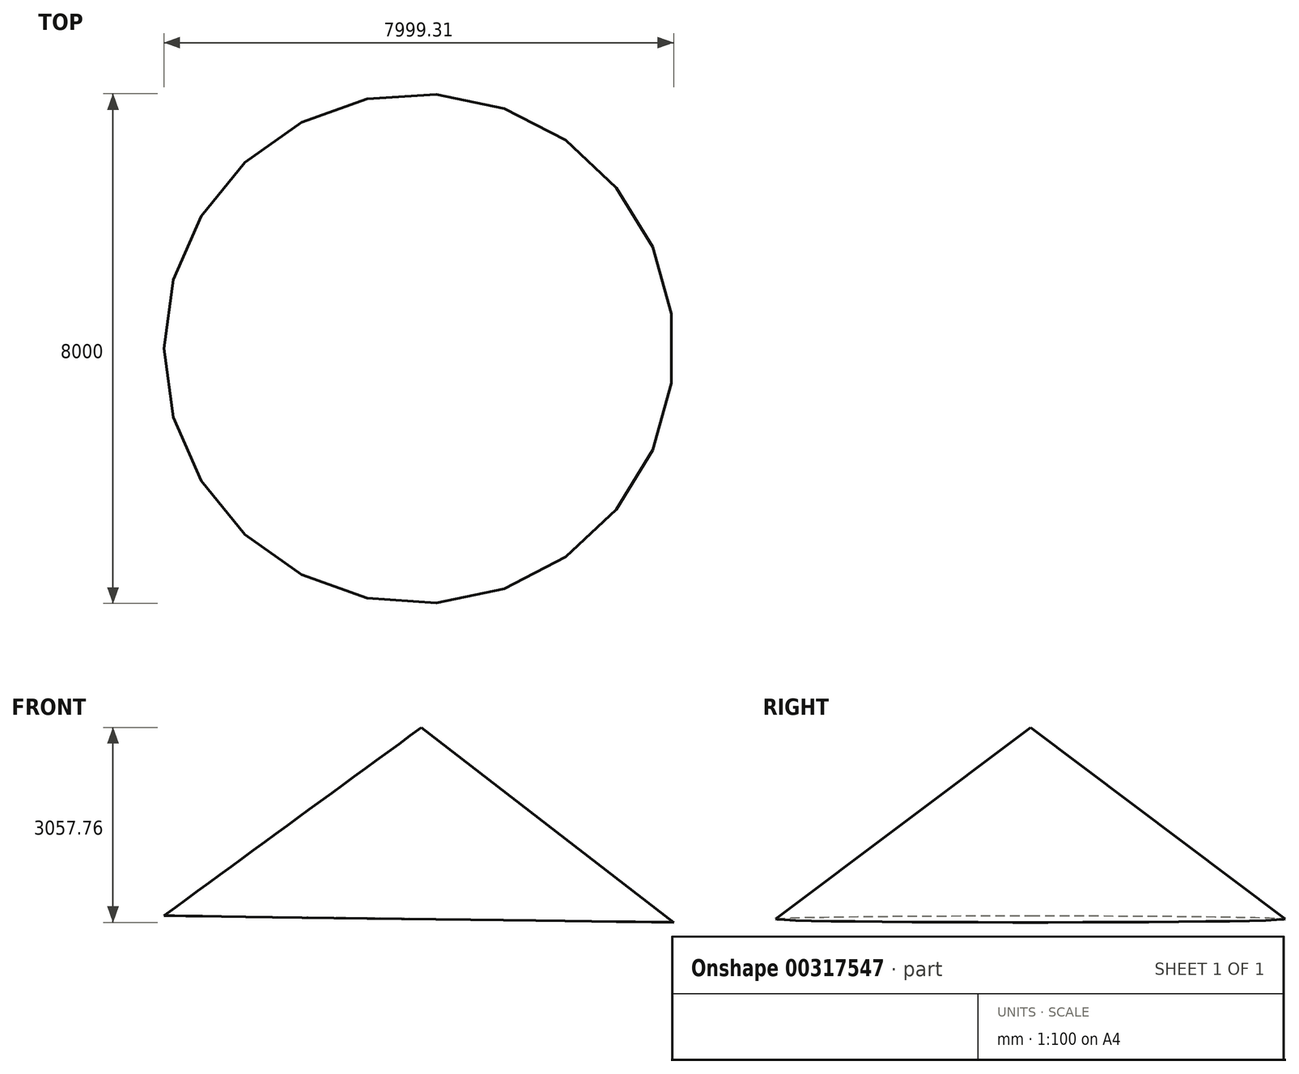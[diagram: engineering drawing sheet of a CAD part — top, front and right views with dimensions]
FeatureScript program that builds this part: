
annotation { "Feature Type Name" : "Feature", "Feature Type Description" : "" }
export const myFeature = defineFeature(function(context is Context, id is Id, definition is map)
    precondition{}
    {
        {
            var Q0;
            Q0=qCreatedBy(makeId("Front.planeOp"),FACE);
            var sketch = newSketch(context, id + "F0", { "sketchPlane" : qUnion([Q0])});
            skLineSegment(sketch, "E0", {"start": v(-48.48, -19.36) * mm, "end": v(-9.18, 2980.64) * mm});
            skLineSegment(sketch, "E1", {"start": v(-9.18, 2980.64) * mm, "end": v(3951.1, -77.12) * mm});
            skLineSegment(sketch, "E2", {"start": v(3951.1, -77.12) * mm, "end": v(-48.48, -19.36) * mm});
            skSolve(sketch);
        }
        {
            var Q0;
            Q0=makeQuery(id+"F0.imprint","IMPRINT",FACE,{"disambiguationData":[TD([[makeQuery(id+"F0.imprint","IMPRINT",EDGE,{"derivedFrom":sQuery(id+"F0.wireOp",EDGE,"E0")}),-1.0]])]});
            var Q1;
            Q1=sQuery(id+"F0.wireOp",EDGE,"E0");
            revolve(context, id + "F1", {"entities" : qUnion([Q0]), "axis" : qUnion([Q1]), "revolveType" : RevolveType.FULL});
        }
    });
